# Revit family: xTowel_Dispenser-Bobrick-ClassicSeries-3944-52
name_source: partatom
category: Specialty Equipment
revit_build: Autodesk Revit 2014 (Build: 20130308_1515(x64)
units: mm (PartAtom-declared; Revit-internal decimal feet)

## types (1)
- 3944-52
    ADA Compliant = Yes
    Assembly Code = E20
    Default Elevation = 44"
    Description = ClassicSeries® Convertible Folded Towel Dispenser Module
    Height = 20 13/16"
    Installation Type = Secured to cabinet.
    Length = 4 1/8"
    Manufacturer = Bobrick Washroom Equipment, Inc.
    Material = Stainless Steel-Bobrick-Type 304-Satin
    Model = 3944-52
    Price = Prices may vary. Please consult Manufacturer Representative for most up-to-date price list.
    Product Documentation Link = http://www.bobrick.com
    Product Page URL = http://www.bobrick.com
    Specification = Convertible folded towel dispenser module shall be type-304 stainless steel with all-welded construction; exposed surfaces shall have satin finish. Door shall be secured to cabinet with a full-length stainless steel piano-hinge and equipped with a semi-concealed tumbler lock keyed like other Bobrick washroom  accessories. Paper towel dispenser shall dispense 600 C-fold or 800 multifold paper towels.
    URL = http://www.bobrick.com
    Warranty Information = 1 Year Limited Warranty
    Width = 15 3/16"

## geometry (parser evidence)
native form markers: Sweep x2
no freeform markers — native parametric forms only
